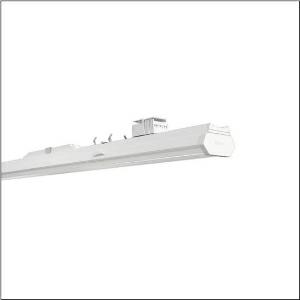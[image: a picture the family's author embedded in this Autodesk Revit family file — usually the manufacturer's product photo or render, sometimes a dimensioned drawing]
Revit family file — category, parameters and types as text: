
# Revit family: licross_r__11_protected_ho_51tp12dn4fxm3s4_aaf8
name_source: partatom
category: Lighting Fixtures
units: mm (PartAtom-declared; Revit-internal decimal feet)

## family parameters
Cut with Voids When Loaded = No
Host = Face
Light Source = No
Part Type = Normal
Room Calculation Point = No
Round Connector Dimension = Use Diameter
Shared = No

## types (1)
- --- (1 x LED, 970 lm, 7.4 W, 4000K)
    Apparent Load = 7 VA
    CIE Flux Codes = 70 91 97 98 100
    Color Rendering = 80
    Color Temperature = 4000K
    Default Elevation = 1800 mm
    Description = Licross® 11 Protected HO, luminaire insert, of sheet steel, galvanised, coil coated, white, length: 1.500mm, width: 90mm, height: 101mm, LED rated luminous flux: 15.270lm, light colour: 840, control gear: DALI 2, with plug, 6-pole, with phase selection, for trunking rail, 9 or 11-core, mains connection: 220..240V, AC, 50/60Hz, rated input power: 91W, for trunking rail, 9-/11-core, internal wiring halogen-free, for emergency light function, converter,control gear: single battery element, battery: LiFePO4, 9Ah, primary light control with lens, of plastic, primary optical cover: cover, of PMMA, light emission: direct distribution, primary light characteristic: symmetric, protection rating (complete): IP64, insulation class (complete): insulation class I (protective earthing), certification: CE, UKCA, protection symbol: D if used in an environment with conductive dust loads with corresponding accessories, impact resistance: IK06, permissible ambient temperature for indoor applications: +5..+30°C, standard: EN 60598-2-22, LABS conformity tested according to VDMA 24364:2018-05, reducing of maximum allowable ambient temperature of 5°C with ceiling mounting, corresponds to IFS (International Featured Standards) requirements for safety and quality in the food industry, packaging unit: 1 piece
    Height = 92 mm
    Lamp = 1 x LED
    Lamp Light Flux = 970 lm
    Lamp Power = 7.4 W
    Lamp count = 1
    Length = 1500 mm
    Luminous efficacy = 131 lm/W
    Manufacturer = Siteco
    ModVariant = No
    Model = 51TP12DN4FXM3S4
    Mounting Place = Ceiling
    Mounting Type = Pendant
    Number of Poles = 1
    OnlyDefault = Yes
    Power Factor = 1
    Product Name = Licross® 11 Protected HO
    Product group = luminaire insert | ceiling pendant
    ProductGroupID = 902
    Protection Class = Protection class I
    Protection Degree = IP 64
    RLX_Detail_Level = 1
    RLX_Emergency_Light_Flux = 0 lm
    RLX_Emergency_Type = 0
    RLX_Emergency_Type_DB = No
    RlxData = <blob elided: 25013 chars, md5=56a755f7>
    Socket = socket
    Standby Power = 0 W
    System Light Flux = 970 lm
    System Power = 7 W
    Type Comments = : emergency light operation: 3 h
    Type Image = l_1256148.jpg
    URL = http://relux.com
    VarID = @adj_112365
    Voltage = 0 V
    Weight = 0.00 kg
    Width = 88 mm

## geometry (parser evidence)
native form markers: Blend x4, Sweep x9
no freeform markers — native parametric forms only
